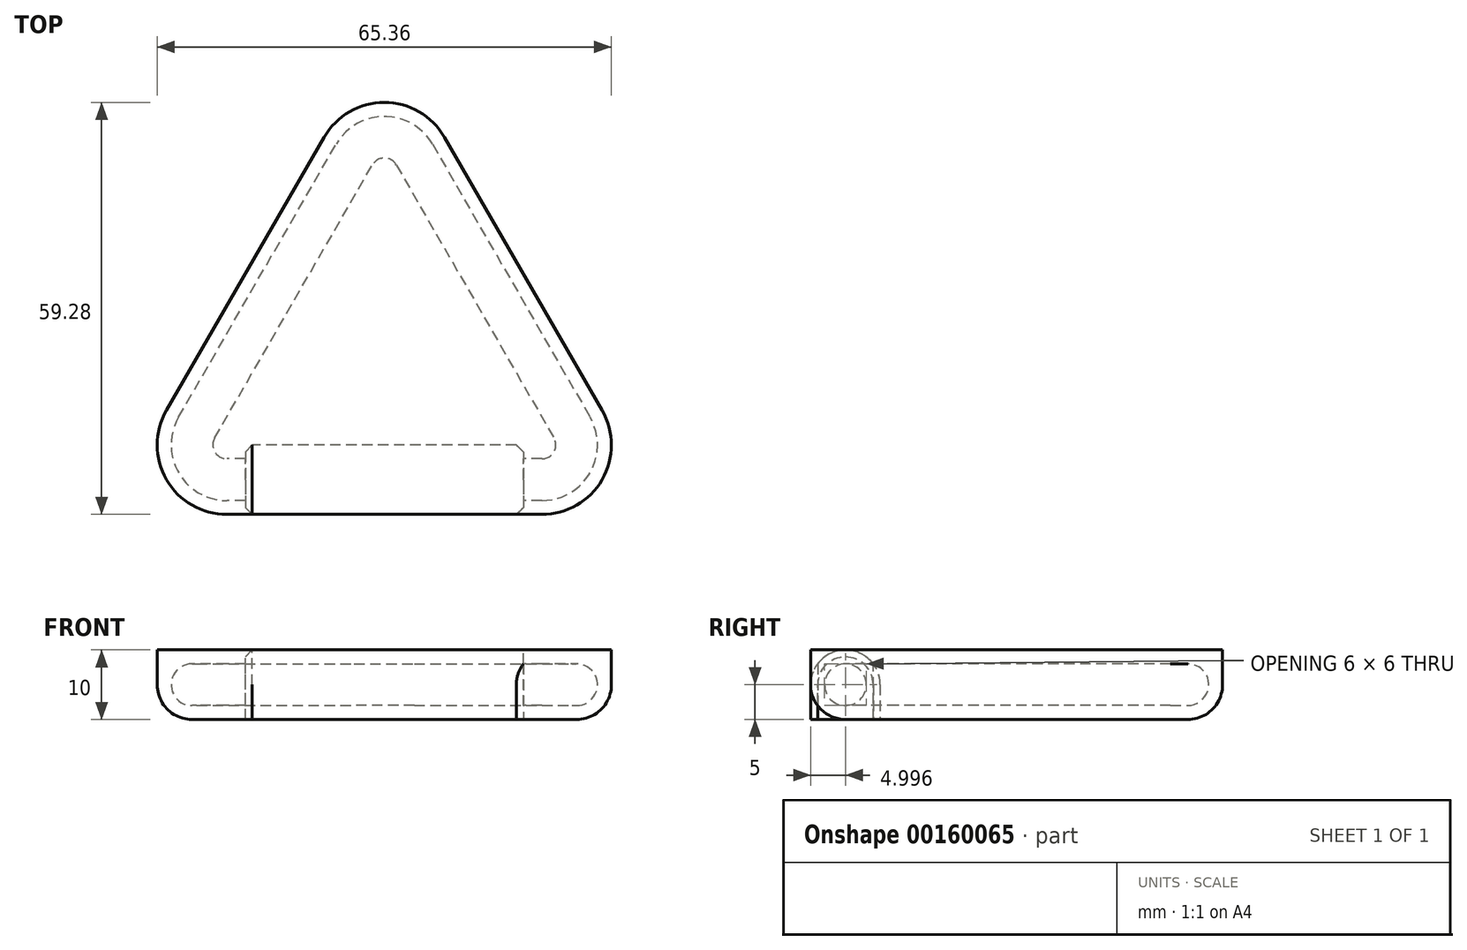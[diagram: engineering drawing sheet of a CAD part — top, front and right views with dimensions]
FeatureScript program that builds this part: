
annotation { "Feature Type Name" : "Feature", "Feature Type Description" : "" }
export const myFeature = defineFeature(function(context is Context, id is Id, definition is map)
    precondition{}
    {
        {
            var Q0;
            Q0=qCreatedBy(makeId("Top.planeOp"),FACE);
            var sketch = newSketch(context, id + "F0", { "sketchPlane" : qUnion([Q0])});
            skCircle(sketch, "E0.cCircle", {"center": v(0, 0) * mm, "radius": 46.19 * mm, "construction": true});
            skLineSegment(sketch, "E0.0", {"start": v(8.66, 31.19) * mm, "end": v(31.34, -8.1) * mm});
            skLineSegment(sketch, "E0.1", {"start": v(22.68, -23.1) * mm, "end": v(-22.68, -23.1) * mm});
            skLineSegment(sketch, "E0.2", {"start": v(-31.34, -8.1) * mm, "end": v(-8.66, 31.19) * mm});
            skPoint(sketch, "E1.visualSharp", {"position": v(0, 46.19) * mm});
            skArc(sketch, "E1.filletArc", {"start": v(8.66, 31.19) * mm, "mid": v(0, 36.19) * mm, "end": v(-8.66, 31.19) * mm});
            skPoint(sketch, "E2.visualSharp", {"position": v(40, -23.1) * mm});
            skArc(sketch, "E2.filletArc", {"start": v(22.68, -23.1) * mm, "mid": v(31.34, -18.1) * mm, "end": v(31.34, -8.1) * mm});
            skPoint(sketch, "E3.visualSharp", {"position": v(-40, -23.1) * mm});
            skArc(sketch, "E3.filletArc", {"start": v(-31.34, -8.1) * mm, "mid": v(-31.34, -18.1) * mm, "end": v(-22.68, -23.1) * mm});
            skSolve(sketch);
        }
        {
            var Q0;
            Q0=makeQuery(id+"F0.imprint","IMPRINT",FACE,{"disambiguationData":[TD([[makeQuery(id+"F0.imprint","IMPRINT",EDGE,{"derivedFrom":sQuery(id+"F0.wireOp",EDGE,"E0.0")}),-1.0]])]});
            var sketch = newSketch(context, id + "F1", { "sketchPlane" : qUnion([Q0])});
            skLineSegment(sketch, "E4.bottom", {"start": v(20, -13.1) * mm, "end": v(-20, -13.1) * mm});
            skLineSegment(sketch, "E4.top", {"start": v(20, -23.1) * mm, "end": v(-20, -23.1) * mm});
            skLineSegment(sketch, "E4.left", {"start": v(20, -13.1) * mm, "end": v(20, -23.1) * mm});
            skLineSegment(sketch, "E4.right", {"start": v(-20, -13.1) * mm, "end": v(-20, -18.1) * mm});
            skPoint(sketch, "E4.middle", {"position": v(0, -18.1) * mm});
            skArc(sketch, "E5.0", {"start": v(22.68, -18.1) * mm, "mid": v(27, -15.6) * mm, "end": v(27, -10.6) * mm});
            skArc(sketch, "E5.1", {"start": v(-27, -10.6) * mm, "mid": v(-27, -15.6) * mm, "end": v(-22.68, -18.1) * mm});
            skLineSegment(sketch, "E5.2", {"start": v(-27, -10.6) * mm, "end": v(-4.33, 28.69) * mm});
            skLineSegment(sketch, "E5.3", {"start": v(22.68, -18.1) * mm, "end": v(-20, -18.1) * mm});
            skArc(sketch, "E5.4", {"start": v(4.33, 28.69) * mm, "mid": v(0, 31.19) * mm, "end": v(-4.33, 28.69) * mm});
            skLineSegment(sketch, "E5.5", {"start": v(4.33, 28.69) * mm, "end": v(27, -10.6) * mm});
            skLineSegment(sketch, "E6", {"start": v(-20, -18.1) * mm, "end": v(-20, -23.1) * mm});
            skLineSegment(sketch, "E7", {"start": v(-20, -18.1) * mm, "end": v(-22.68, -18.1) * mm});
            skSolve(sketch);
        }
        {
            var Q0;
            {var subQ0=sQuery(id+"F1.wireOp",EDGE,"E4.top");Q0=makeQuery(id+"F1.imprint","IMPRINT",FACE,{"disambiguationData":[TD([[makeQuery(id+"F1.imprint","IMPRINT",EDGE,{"derivedFrom":subQ0}),-1.0]])]});}
            var Q1;
            {var subQ0=sQuery(id+"F1.wireOp",EDGE,"E4.bottom");Q1=makeQuery(id+"F1.imprint","IMPRINT",FACE,{"disambiguationData":[TD([[makeQuery(id+"F1.imprint","IMPRINT",EDGE,{"derivedFrom":subQ0}),1.0]])]});}
            extrude(context, id + "F2", {"entities" : qUnion([Q0, Q1]), "depth" : 5 * mm});
        }
        {
            var Q0;
            Q0=makeQuery(id+"F2.opExtrude","SWEPT_FACE",FACE,{"disambiguationData":[OSD([sQuery(id+"F1.wireOp",EDGE,"E4.right"),sQuery(id+"F1.wireOp",EDGE,"E6")])]});
            var sketch = newSketch(context, id + "F3", { "sketchPlane" : qUnion([Q0])});
            skCircle(sketch, "E8", {"center": v(18.1, 5) * mm, "radius": 5 * mm});
            skCircle(sketch, "E9", {"center": v(18.1, 5) * mm, "radius": 3 * mm});
            skSolve(sketch);
        }
        {
            var Q0;
            {var subQ1=sQuery(id+"F1.wireOp",EDGE,"E6");var subQ2=sQuery(id+"F1.wireOp",EDGE,"E4.right");var subQ3=makeQuery(id+"F2.opExtrude","CAP_EDGE",EDGE,{"disambiguationData":[OSD([subQ2,subQ1])],"isStart":false});var subQ6=sQuery(id+"F3.wireOp",EDGE,"E9");var subQ7=makeQuery(id+"F3.imprint","INTERSECT",VERTEX,{"disambiguationData":[OD(0.0)],"derivedFrom":[subQ3,subQ6]});Q0=makeQuery(id+"F3.imprint","IMPRINT",FACE,{"disambiguationData":[TD([[makeQuery(id+"F3.imprint","IMPRINT",EDGE,{"disambiguationData":[TD([[subQ7,1.0]])],"derivedFrom":subQ6}),-1.0]])]});}
            var Q1;
            {var subQ0=sQuery(id+"F3.wireOp",EDGE,"E9");var subQ1=makeQuery(id+"F2.opExtrude","CAP_EDGE",EDGE,{"disambiguationData":[OSD([sQuery(id+"F1.wireOp",EDGE,"E4.right"),sQuery(id+"F1.wireOp",EDGE,"E6")])],"isStart":false});var subQ2=makeQuery(id+"F3.imprint","INTERSECT",VERTEX,{"disambiguationData":[OD(0.0)],"derivedFrom":[subQ1,subQ0]});Q1=makeQuery(id+"F3.imprint","IMPRINT",FACE,{"disambiguationData":[TD([[makeQuery(id+"F3.imprint","IMPRINT",EDGE,{"disambiguationData":[TD([[subQ2,1.0]])],"derivedFrom":subQ0}),1.0]])]});}
            var Q2;
            Q2=makeQuery(id+"F2.opExtrude","SWEPT_FACE",FACE,{"disambiguationData":[OSD([sQuery(id+"F1.wireOp",EDGE,"E4.left")])]});
            extrude(context, id + "F4", {"entities" : qUnion([Q0, Q1]), "operationType" : NewBodyOperationType.ADD, "endBound" : BoundingType.UP_TO_SURFACE, "oppositeDirection" : true, "endBoundEntityFace" : qUnion([Q2]), "depth" : 25 * mm});
        }
        {
            var Q0;
            {var subQ0=sQuery(id+"F3.wireOp",EDGE,"E9");var subQ1=makeQuery(id+"F2.opExtrude","CAP_EDGE",EDGE,{"disambiguationData":[OSD([sQuery(id+"F1.wireOp",EDGE,"E4.right"),sQuery(id+"F1.wireOp",EDGE,"E6")])],"isStart":false});var subQ2=makeQuery(id+"F3.imprint","INTERSECT",VERTEX,{"disambiguationData":[OD(0.0)],"derivedFrom":[subQ1,subQ0]});Q0=makeQuery(id+"F3.imprint","IMPRINT",FACE,{"disambiguationData":[TD([[makeQuery(id+"F3.imprint","IMPRINT",EDGE,{"disambiguationData":[TD([[subQ2,-1.0]])],"derivedFrom":subQ0}),1.0]])]});}
            var Q1;
            {var subQ0=sQuery(id+"F3.wireOp",EDGE,"E9");var subQ1=makeQuery(id+"F2.opExtrude","CAP_EDGE",EDGE,{"disambiguationData":[OSD([sQuery(id+"F1.wireOp",EDGE,"E4.right"),sQuery(id+"F1.wireOp",EDGE,"E6")])],"isStart":false});var subQ2=makeQuery(id+"F3.imprint","INTERSECT",VERTEX,{"disambiguationData":[OD(0.0)],"derivedFrom":[subQ1,subQ0]});Q1=makeQuery(id+"F3.imprint","IMPRINT",FACE,{"disambiguationData":[TD([[makeQuery(id+"F3.imprint","IMPRINT",EDGE,{"disambiguationData":[TD([[subQ2,1.0]])],"derivedFrom":subQ0}),1.0]])]});}
            var Q2;
            Q2=sQuery(id+"F1.wireOp",EDGE,"E7");
            var Q3;
            Q3=sQuery(id+"F1.wireOp",EDGE,"E5.1");
            var Q4;
            Q4=sQuery(id+"F1.wireOp",EDGE,"E5.2");
            var Q5;
            Q5=sQuery(id+"F1.wireOp",EDGE,"E5.4");
            var Q6;
            Q6=sQuery(id+"F1.wireOp",EDGE,"E5.5");
            var Q7;
            Q7=sQuery(id+"F1.wireOp",EDGE,"E5.0");
            var Q8;
            Q8=sQuery(id+"F1.wireOp",EDGE,"E5.3");
            sweep(context, id + "F5", {"operationType" : NewBodyOperationType.ADD, "profiles" : qUnion([Q0, Q1]), "path" : qUnion([Q2, Q3, Q4, Q5, Q6, Q7, Q8])});
        }
        {
            var Q0;
            Q0=makeQuery(id+"F0.imprint","IMPRINT",FACE,{"disambiguationData":[TD([[makeQuery(id+"F0.imprint","IMPRINT",EDGE,{"derivedFrom":sQuery(id+"F0.wireOp",EDGE,"E0.0")}),-1.0]])]});
            extrude(context, id + "F6", {"entities" : qUnion([Q0]), "depth" : 10 * mm});
        }
        {
            var Q0;
            Q0=makeQuery(id+"F6.opExtrude","CAP_EDGE",EDGE,{"disambiguationData":[OSD([sQuery(id+"F0.wireOp",EDGE,"E0.2")])],"isStart":true});
            fillet(context, id + "F7", {"entities" : qUnion([Q0]), "radius" : 5 * mm, "tangentPropagation" : true, "allowEdgeOverflow" : false});
        }
        {
            var Q0;
            Q0=makeQuery(id+"F2.opExtrude","SWEPT_EDGE",EDGE,{"disambiguationData":[OSD([sQuery(id+"F0.wireOp",EDGE,"E0.1"),sQuery(id+"F1.wireOp",EDGE,"E4.top"),sQuery(id+"F1.wireOp",EDGE,"E4.left")])]});
            var Q1;
            {var subQ0=sQuery(id+"F3.wireOp",EDGE,"E8");var subQ1=sQuery(id+"F1.wireOp",EDGE,"E6");var subQ2=sQuery(id+"F1.wireOp",EDGE,"E4.right");var subQ3=makeQuery(id+"F2.opExtrude","CAP_EDGE",EDGE,{"disambiguationData":[OSD([subQ2,subQ1])],"isStart":false});Q1=makeQuery(id+"F4.opExtrude","TWEAK_EDGE",EDGE,{"derivedFrom":[makeQuery(id+"F2.opExtrude","SWEPT_FACE",FACE,{"disambiguationData":[OSD([sQuery(id+"F1.wireOp",EDGE,"E4.left")])]}),makeQuery(id+"F3.imprint","IMPRINT",EDGE,{"disambiguationData":[TD([[makeQuery(id+"F3.imprint","INTERSECT",VERTEX,{"derivedFrom":[makeQuery(id+"F2.opExtrude","SWEPT_EDGE",EDGE,{"disambiguationData":[OSD([sQuery(id+"F1.wireOp",EDGE,"E4.bottom"),subQ2])]}),subQ3,subQ0]}),1.0]])],"derivedFrom":subQ0})]});}
            var Q2;
            Q2=makeQuery(id+"F2.opExtrude","SWEPT_EDGE",EDGE,{"disambiguationData":[OSD([sQuery(id+"F1.wireOp",EDGE,"E4.bottom"),sQuery(id+"F1.wireOp",EDGE,"E4.left")])]});
            var Q3;
            Q3=makeQuery(id+"F2.opExtrude","SWEPT_EDGE",EDGE,{"disambiguationData":[OSD([sQuery(id+"F1.wireOp",EDGE,"E4.bottom"),sQuery(id+"F1.wireOp",EDGE,"E4.right")])]});
            var Q4;
            Q4=makeQuery(id+"F4.opExtrude","CAP_EDGE",EDGE,{"disambiguationData":[OSD([sQuery(id+"F3.wireOp",EDGE,"E8")])],"isStart":true});
            var Q5;
            Q5=makeQuery(id+"F2.opExtrude","SWEPT_EDGE",EDGE,{"disambiguationData":[OSD([sQuery(id+"F0.wireOp",EDGE,"E0.1"),sQuery(id+"F1.wireOp",EDGE,"E4.top"),sQuery(id+"F1.wireOp",EDGE,"E6")])]});
            chamfer(context, id + "F8", {"entities" : qUnion([Q0, Q1, Q2, Q3, Q4, Q5]), "width" : 1 * mm});
        }
    });
